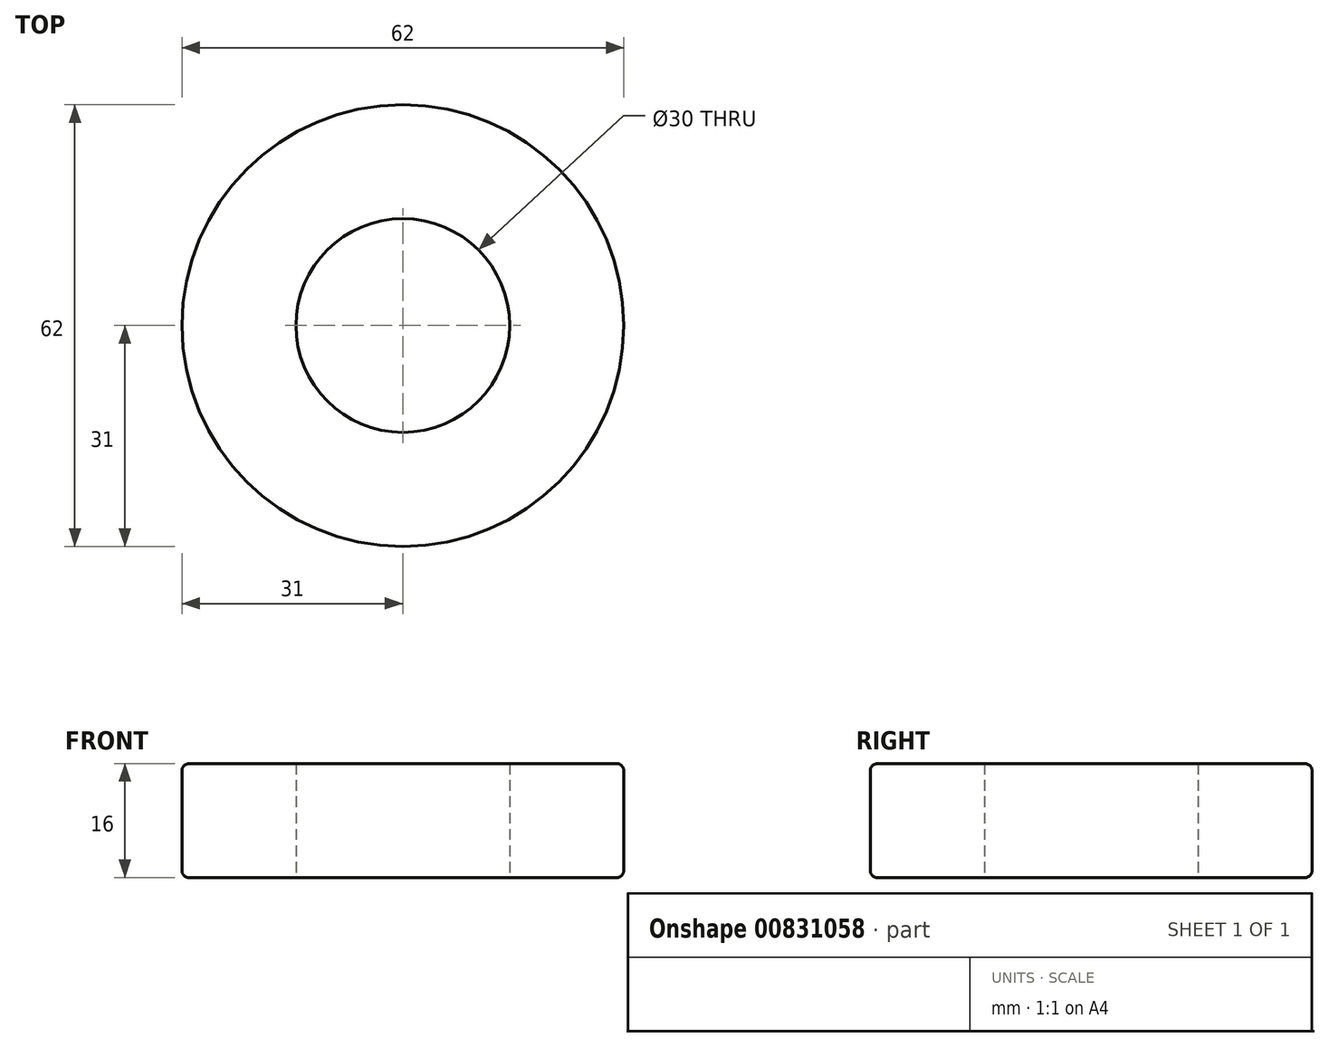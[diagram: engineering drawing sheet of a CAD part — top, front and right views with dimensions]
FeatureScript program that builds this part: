
annotation { "Feature Type Name" : "Feature", "Feature Type Description" : "" }
export const myFeature = defineFeature(function(context is Context, id is Id, definition is map)
    precondition{}
    {
        {
            var Q0;
            Q0=qCreatedBy(makeId("Top.planeOp"),FACE);
            var sketch = newSketch(context, id + "F0", { "sketchPlane" : qUnion([Q0])});
            skCircle(sketch, "E0", {"center": v(0, 0) * mm, "radius": 31 * mm});
            skCircle(sketch, "E1", {"center": v(0, 0) * mm, "radius": 15 * mm});
            skSolve(sketch);
        }
        {
            var Q0;
            Q0=makeQuery(id+"F0.imprint","IMPRINT",FACE,{"disambiguationData":[TD([[makeQuery(id+"F0.imprint","IMPRINT",EDGE,{"derivedFrom":sQuery(id+"F0.wireOp",EDGE,"E0")}),1.0]])]});
            extrude(context, id + "F1", {"entities" : qUnion([Q0]), "depth" : 16 * mm, "offsetDistance" : 25 * mm});
        }
        {
            var Q0;
            Q0=makeQuery(id+"F1.opExtrude","CAP_EDGE",EDGE,{"disambiguationData":[OSD([sQuery(id+"F0.wireOp",EDGE,"E0")])],"isStart":false});
            var Q1;
            Q1=makeQuery(id+"F1.opExtrude","SWEPT_FACE",FACE,{"disambiguationData":[OSD([sQuery(id+"F0.wireOp",EDGE,"E0")])]});
            fillet(context, id + "F2", {"entities" : qUnion([Q0, Q1]), "radius" : 1 * mm, "tangentPropagation" : true, "allowEdgeOverflow" : false});
        }
    });
